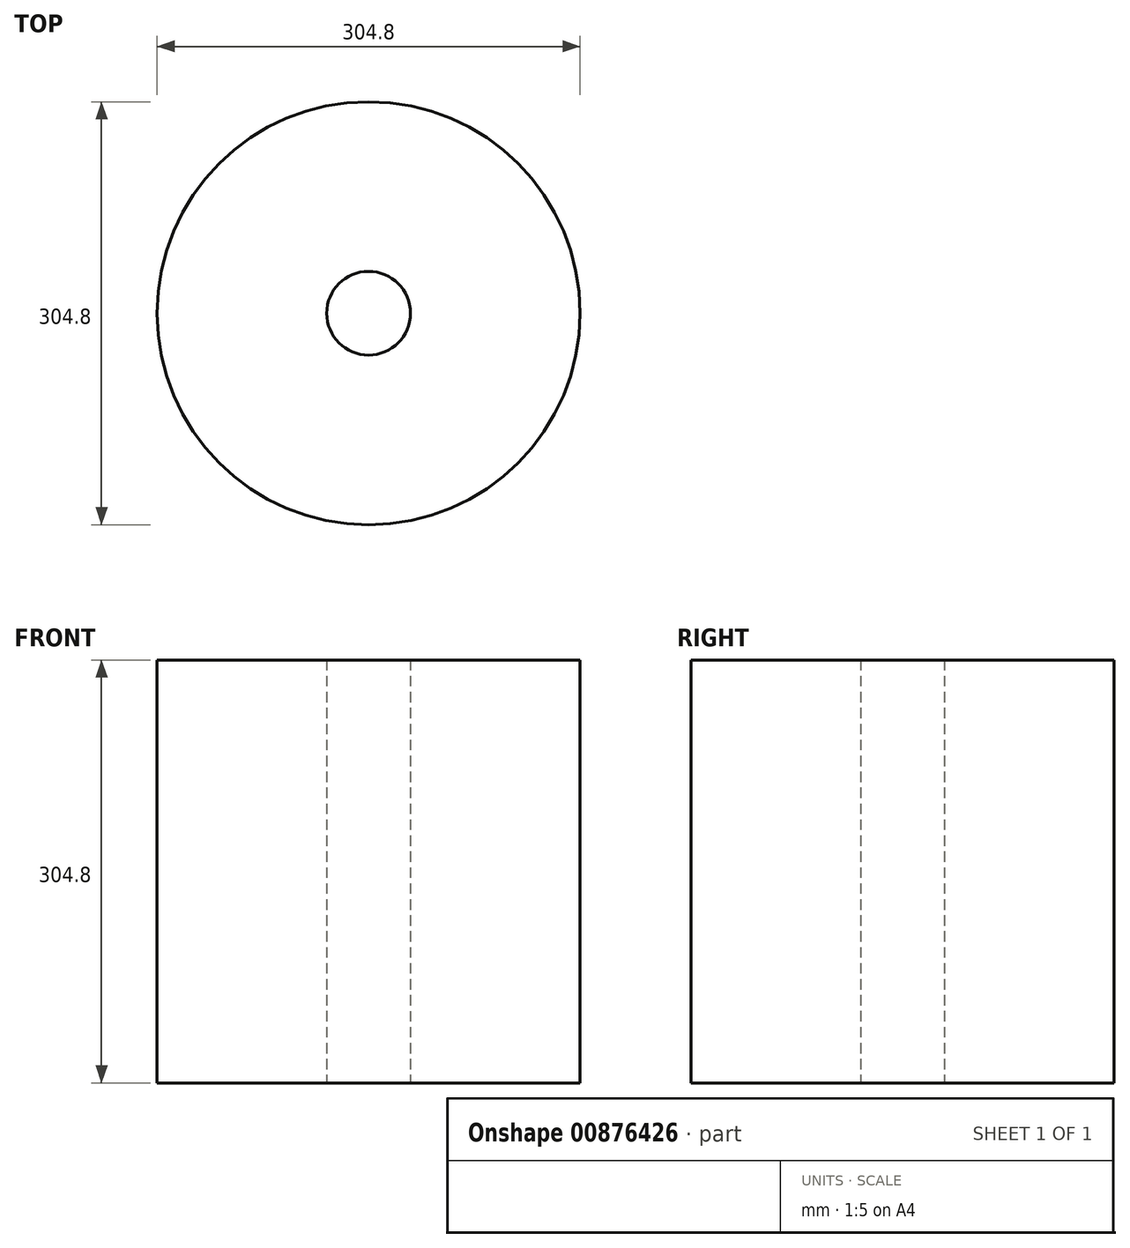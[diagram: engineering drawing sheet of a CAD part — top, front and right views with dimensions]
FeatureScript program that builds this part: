
annotation { "Feature Type Name" : "Feature", "Feature Type Description" : "" }
export const myFeature = defineFeature(function(context is Context, id is Id, definition is map)
    precondition{}
    {
        {
            var Q0;
            Q0=qCreatedBy(makeId("Top.planeOp"),FACE);
            var sketch = newSketch(context, id + "F0", { "sketchPlane" : qUnion([Q0])});
            skCircle(sketch, "E0", {"center": v(0, 0) * mm, "radius": 30.16 * mm});
            skCircle(sketch, "E1", {"center": v(0, 0) * mm, "radius": 152.4 * mm});
            skSolve(sketch);
        }
        {
            var Q0;
            Q0=makeQuery(id+"F0.imprint","IMPRINT",FACE,{"disambiguationData":[TD([[makeQuery(id+"F0.imprint","IMPRINT",EDGE,{"derivedFrom":sQuery(id+"F0.wireOp",EDGE,"E0")}),-1.0]])]});
            extrude(context, id + "F1", {"entities" : qUnion([Q0]), "depth" : 304.8 * mm, "offsetDistance" : 25.4 * mm});
        }
    });
